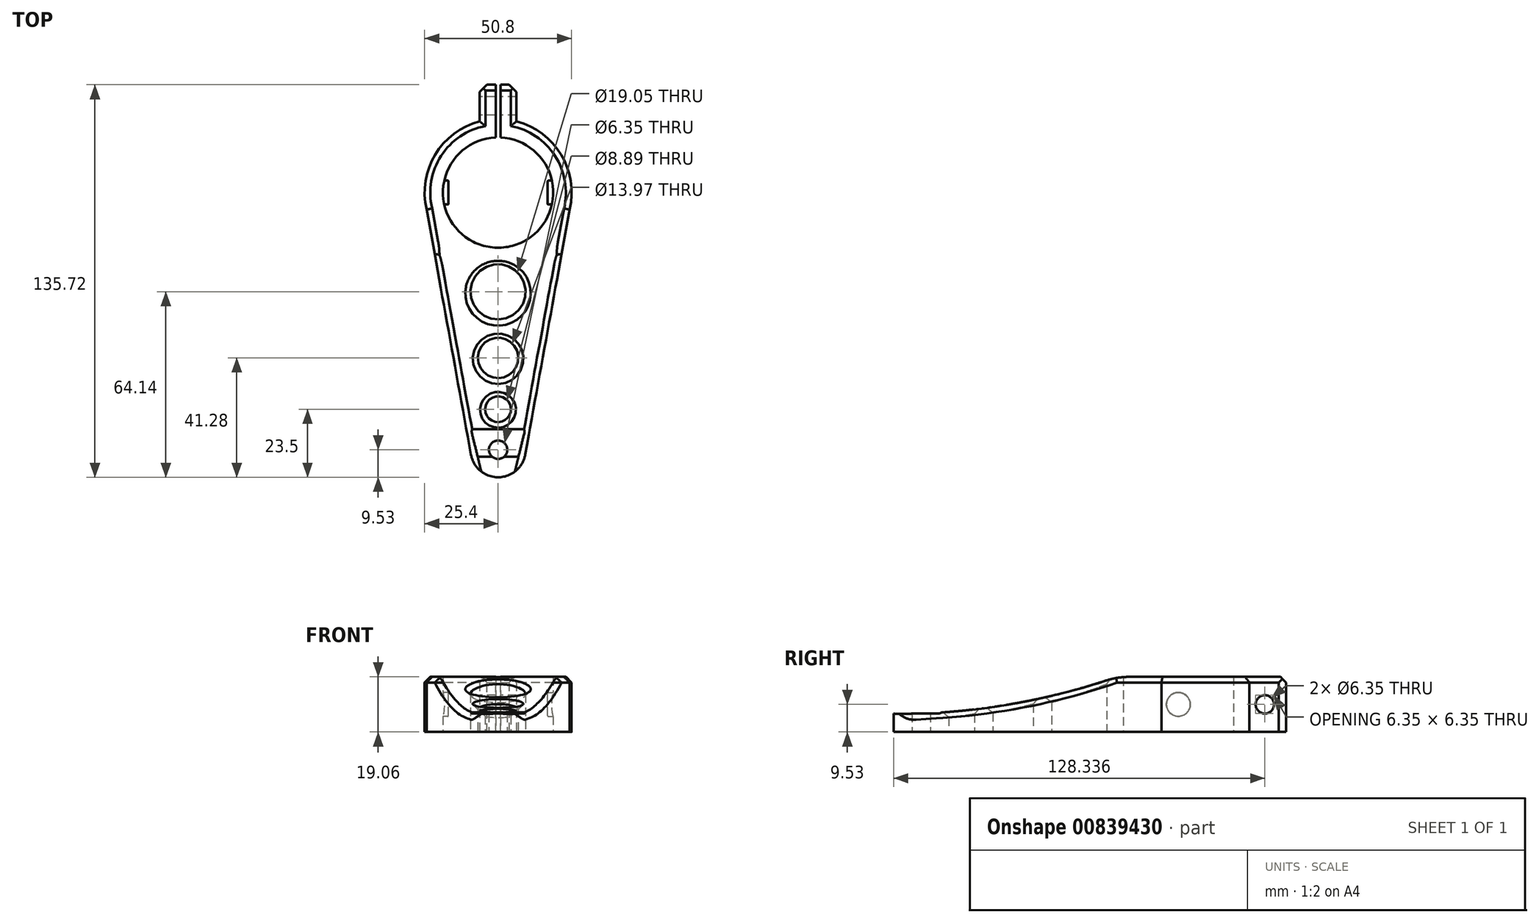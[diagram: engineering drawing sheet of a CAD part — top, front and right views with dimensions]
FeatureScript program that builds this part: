
annotation { "Feature Type Name" : "Feature", "Feature Type Description" : "" }
export const myFeature = defineFeature(function(context is Context, id is Id, definition is map)
    precondition{}
    {
        {
            var Q0;
            Q0=qCreatedBy(makeId("Top.planeOp"),FACE);
            var sketch = newSketch(context, id + "F0", { "sketchPlane" : qUnion([Q0])});
            skCircle(sketch, "E0", {"center": v(0, 0) * mm, "radius": 19.05 * mm});
            skCircle(sketch, "E1", {"center": v(0, 0) * mm, "radius": 25.4 * mm});
            skLineSegment(sketch, "E2", {"start": v(0, 0) * mm, "end": v(0, -88.9) * mm, "construction": true});
            skCircle(sketch, "E3", {"center": v(0, -88.9) * mm, "radius": 3.18 * mm});
            skCircle(sketch, "E4", {"center": v(0, -88.9) * mm, "radius": 9.53 * mm});
            skLineSegment(sketch, "E5", {"start": v(-24.71, -5.87) * mm, "end": v(-9.37, -90.6) * mm});
            skLineSegment(sketch, "E6.MirrorCS", {"start": v(24.71, -5.87) * mm, "end": v(9.37, -90.6) * mm});
            skCircle(sketch, "E7", {"center": v(0, -34.29) * mm, "radius": 9.53 * mm});
            skCircle(sketch, "E8", {"center": v(0, -57.15) * mm, "radius": 6.99 * mm});
            skCircle(sketch, "E9", {"center": v(0, -74.93) * mm, "radius": 4.45 * mm});
            skLineSegment(sketch, "E10", {"start": v(0, 0) * mm, "end": v(0, 30.94) * mm, "construction": true});
            skLineSegment(sketch, "E11.bottom", {"start": v(6.35, 24.6) * mm, "end": v(-6.35, 24.6) * mm});
            skLineSegment(sketch, "E11.top", {"start": v(6.35, 37.3) * mm, "end": v(-6.35, 37.3) * mm});
            skLineSegment(sketch, "E11.left", {"start": v(6.35, 24.6) * mm, "end": v(6.35, 37.3) * mm});
            skLineSegment(sketch, "E11.right", {"start": v(-6.35, 24.6) * mm, "end": v(-6.35, 37.3) * mm});
            skPoint(sketch, "E11.middle", {"position": v(0, 30.94) * mm});
            skSolve(sketch);
        }
        {
            var Q0;
            Q0 = qSketchRegion(id + "F0", true);
            extrude(context, id + "F1", {"entities" : qUnion([Q0]), "depth" : 19.05 * mm, "offsetDistance" : 25.4 * mm, "symmetric" : true});
        }
        {
            var Q0;
            Q0=qCreatedBy(makeId("Right.planeOp"),FACE);
            var sketch = newSketch(context, id + "F2", { "sketchPlane" : qUnion([Q0])});
            skLineSegment(sketch, "E12", {"start": v(0, 0) * mm, "end": v(-12.7, 0) * mm, "construction": true});
            skLineSegment(sketch, "E13", {"start": v(-12.7, 0) * mm, "end": v(-12.7, 12.7) * mm, "construction": true});
            skLineSegment(sketch, "E14", {"start": v(-12.7, 0) * mm, "end": v(-12.7, -12.7) * mm, "construction": true});
            skFitSpline(sketch, "E15", {"points": [v(-12.7, 12.7) * mm, v(-99.37, -3.18) * mm], "startDerivative": vector(-81.6, -32.58) * mm, "endDerivative": vector(-83.24, 1.78) * mm});
            skLineSegment(sketch, "E16", {"start": v(-99.37, -3.18) * mm, "end": v(-99.37, 12.7) * mm});
            skLineSegment(sketch, "E17", {"start": v(-99.37, 12.7) * mm, "end": v(-12.7, 12.7) * mm});
            skLineSegment(sketch, "E18.bottom", {"start": v(-81.84, 19.28) * mm, "end": v(-103.5, 19.28) * mm});
            skLineSegment(sketch, "E18.top", {"start": v(-81.84, -3.18) * mm, "end": v(-103.5, -3.18) * mm});
            skLineSegment(sketch, "E18.left", {"start": v(-81.84, 19.28) * mm, "end": v(-81.84, -3.17) * mm});
            skLineSegment(sketch, "E18.right", {"start": v(-103.5, 19.28) * mm, "end": v(-103.5, -3.18) * mm});
            skSolve(sketch);
        }
        {
            var Q0;
            Q0 = qSketchRegion(id + "F2", true);
            extrude(context, id + "F3", {"entities" : qUnion([Q0]), "operationType" : NewBodyOperationType.REMOVE, "endBound" : BoundingType.THROUGH_ALL, "oppositeDirection" : true, "depth" : 25.4 * mm, "offsetDistance" : 25.4 * mm, "hasSecondDirection" : true, "secondDirectionBound" : BoundingType.THROUGH_ALL, "secondDirectionOppositeDirection" : false, "secondDirectionDepth" : 25.4 * mm});
        }
        {
            var Q0;
            Q0=makeQuery(id+"F3.boolean.opBoolean","INTERSECT",EDGE,{"derivedFrom":[makeQuery(id+"F1.opExtrude","SWEPT_FACE",FACE,{"disambiguationData":[OSD([sQuery(id+"F0.wireOp",EDGE,"E5")])]}),makeQuery(id+"F3.opExtrude","SWEPT_FACE",FACE,{"disambiguationData":[OSD([sQuery(id+"F2.wireOp",EDGE,"E15")])]})]});
            var Q1;
            Q1=makeQuery(id+"F1.opExtrude","CAP_EDGE",EDGE,{"disambiguationData":[OSD([sQuery(id+"F0.wireOp",EDGE,"E5")])],"isStart":false});
            var Q2;
            {var subQ0=sQuery(id+"F0.wireOp",EDGE,"E1");Q2=makeQuery(id+"F1.opExtrude","CAP_EDGE",EDGE,{"disambiguationData":[OSD([subQ0]),TDD([makeQuery(id+"F0.imprint","IMPRINT",EDGE,{"disambiguationData":[TD([[makeQuery(id+"F0.imprint","INTERSECT",VERTEX,{"derivedFrom":[subQ0,sQuery(id+"F0.wireOp",EDGE,"E5")]}),1.0]])],"derivedFrom":subQ0})])],"isStart":false});}
            var Q3;
            Q3=makeQuery(id+"F1.opExtrude","CAP_EDGE",EDGE,{"disambiguationData":[OSD([sQuery(id+"F0.wireOp",EDGE,"E11.right")])],"isStart":false});
            var Q4;
            Q4=makeQuery(id+"F1.opExtrude","CAP_EDGE",EDGE,{"disambiguationData":[OSD([sQuery(id+"F0.wireOp",EDGE,"E11.top")])],"isStart":false});
            var Q5;
            Q5=makeQuery(id+"F1.opExtrude","CAP_EDGE",EDGE,{"disambiguationData":[OSD([sQuery(id+"F0.wireOp",EDGE,"E11.left")])],"isStart":false});
            var Q6;
            {var subQ0=sQuery(id+"F0.wireOp",EDGE,"E1");Q6=makeQuery(id+"F1.opExtrude","CAP_EDGE",EDGE,{"disambiguationData":[OSD([subQ0]),TDD([makeQuery(id+"F0.imprint","IMPRINT",EDGE,{"disambiguationData":[TD([[makeQuery(id+"F0.imprint","INTERSECT",VERTEX,{"derivedFrom":[subQ0,sQuery(id+"F0.wireOp",EDGE,"E6.MirrorCS")]}),-1.0]])],"derivedFrom":subQ0})])],"isStart":false});}
            var Q7;
            Q7=makeQuery(id+"F1.opExtrude","CAP_EDGE",EDGE,{"disambiguationData":[OSD([sQuery(id+"F0.wireOp",EDGE,"E6.MirrorCS")])],"isStart":false});
            var Q8;
            {var subQ0=sQuery(id+"F2.wireOp",EDGE,"E15");Q8=makeQuery(id+"F3.boolean.opBoolean","INTERSECT",EDGE,{"derivedFrom":[makeQuery(id+"F1.opExtrude","SWEPT_FACE",FACE,{"disambiguationData":[OSD([sQuery(id+"F0.wireOp",EDGE,"E6.MirrorCS")])]}),makeQuery(id+"F3.opExtrude","SWEPT_FACE",FACE,{"disambiguationData":[OSD([subQ0]),TDD([makeQuery(id+"F2.imprint","IMPRINT",EDGE,{"disambiguationData":[TD([[makeQuery(id+"F2.imprint","INTERSECT",VERTEX,{"derivedFrom":[subQ0,sQuery(id+"F2.wireOp",EDGE,"E17")]}),-1.0]])],"derivedFrom":subQ0})])]})]});}
            chamfer(context, id + "F4", {"entities" : qUnion([Q0, Q1, Q2, Q3, Q4, Q5, Q6, Q7, Q8]), "width" : 1.9 * mm, "tangentPropagation" : true});
        }
        {
            var Q0;
            Q0=makeQuery(id+"F1.opExtrude","SWEPT_EDGE",EDGE,{"disambiguationData":[OSD([sQuery(id+"F0.wireOp",EDGE,"E11.top"),sQuery(id+"F0.wireOp",EDGE,"E11.right")])]});
            var Q1;
            Q1=makeQuery(id+"F1.opExtrude","SWEPT_EDGE",EDGE,{"disambiguationData":[OSD([sQuery(id+"F0.wireOp",EDGE,"E11.top"),sQuery(id+"F0.wireOp",EDGE,"E11.left")])]});
            chamfer(context, id + "F5", {"entities" : qUnion([Q0, Q1]), "width" : 2.54 * mm, "tangentPropagation" : true});
        }
        {
            var Q0;
            Q0=qCreatedBy(makeId("Right.planeOp"),FACE);
            var sketch = newSketch(context, id + "F6", { "sketchPlane" : qUnion([Q0])});
            skLineSegment(sketch, "E19.bottom", {"start": v(48.1, -21.83) * mm, "end": v(8.61, -21.83) * mm});
            skLineSegment(sketch, "E19.top", {"start": v(48.1, 18.76) * mm, "end": v(8.61, 18.76) * mm});
            skLineSegment(sketch, "E19.left", {"start": v(48.1, -21.83) * mm, "end": v(48.1, 18.76) * mm});
            skLineSegment(sketch, "E19.right", {"start": v(8.61, -21.83) * mm, "end": v(8.61, 18.76) * mm});
            skSolve(sketch);
        }
        {
            var Q0;
            Q0 = qSketchRegion(id + "F6", true);
            extrude(context, id + "F7", {"entities" : qUnion([Q0]), "operationType" : NewBodyOperationType.REMOVE, "oppositeDirection" : true, "depth" : 1.65 * mm, "offsetDistance" : 25.4 * mm, "symmetric" : true});
        }
        {
            var Q0;
            Q0=makeQuery(id+"F3.boolean.opBoolean","INTERSECT",EDGE,{"derivedFrom":[makeQuery(id+"F1.opExtrude","SWEPT_FACE",FACE,{"disambiguationData":[OSD([sQuery(id+"F0.wireOp",EDGE,"E7")])]}),makeQuery(id+"F3.opExtrude","SWEPT_FACE",FACE,{"disambiguationData":[OSD([sQuery(id+"F2.wireOp",EDGE,"E15")])]})]});
            var Q1;
            Q1=makeQuery(id+"F3.boolean.opBoolean","INTERSECT",EDGE,{"derivedFrom":[makeQuery(id+"F1.opExtrude","SWEPT_FACE",FACE,{"disambiguationData":[OSD([sQuery(id+"F0.wireOp",EDGE,"E8")])]}),makeQuery(id+"F3.opExtrude","SWEPT_FACE",FACE,{"disambiguationData":[OSD([sQuery(id+"F2.wireOp",EDGE,"E15")])]})]});
            var Q2;
            Q2=makeQuery(id+"F3.boolean.opBoolean","INTERSECT",EDGE,{"derivedFrom":[makeQuery(id+"F1.opExtrude","SWEPT_FACE",FACE,{"disambiguationData":[OSD([sQuery(id+"F0.wireOp",EDGE,"E9")])]}),makeQuery(id+"F3.opExtrude","SWEPT_FACE",FACE,{"disambiguationData":[OSD([sQuery(id+"F2.wireOp",EDGE,"E15")])]})]});
            var Q3;
            Q3=makeQuery(id+"F3.boolean.opBoolean","INTERSECT",EDGE,{"derivedFrom":[makeQuery(id+"F1.opExtrude","SWEPT_FACE",FACE,{"disambiguationData":[OSD([sQuery(id+"F0.wireOp",EDGE,"E7")])]}),makeQuery(id+"F3.opExtrude","SWEPT_FACE",FACE,{"disambiguationData":[OSD([sQuery(id+"F2.wireOp",EDGE,"91bf1d3f-22a0-42a9-8744-9027ca880ea70.MirrorCS")])]})]});
            var Q4;
            Q4=makeQuery(id+"F3.boolean.opBoolean","INTERSECT",EDGE,{"derivedFrom":[makeQuery(id+"F1.opExtrude","SWEPT_FACE",FACE,{"disambiguationData":[OSD([sQuery(id+"F0.wireOp",EDGE,"E8")])]}),makeQuery(id+"F3.opExtrude","SWEPT_FACE",FACE,{"disambiguationData":[OSD([sQuery(id+"F2.wireOp",EDGE,"91bf1d3f-22a0-42a9-8744-9027ca880ea70.MirrorCS")])]})]});
            var Q5;
            Q5=makeQuery(id+"F3.boolean.opBoolean","INTERSECT",EDGE,{"derivedFrom":[makeQuery(id+"F1.opExtrude","SWEPT_FACE",FACE,{"disambiguationData":[OSD([sQuery(id+"F0.wireOp",EDGE,"E9")])]}),makeQuery(id+"F3.opExtrude","SWEPT_FACE",FACE,{"disambiguationData":[OSD([sQuery(id+"F2.wireOp",EDGE,"91bf1d3f-22a0-42a9-8744-9027ca880ea70.MirrorCS")])]})]});
            chamfer(context, id + "F8", {"entities" : qUnion([Q0, Q1, Q2, Q3, Q4, Q5]), "width" : 1.78 * mm, "tangentPropagation" : true});
        }
        {
            var Q0;
            Q0=makeQuery(id+"F1.opExtrude","SWEPT_FACE",FACE,{"disambiguationData":[OSD([sQuery(id+"F0.wireOp",EDGE,"E11.right")])]});
            var sketch = newSketch(context, id + "F9", { "sketchPlane" : qUnion([Q0])});
            skCircle(sketch, "E20", {"center": v(-29.9, 0) * mm, "radius": 3.18 * mm});
            skSolve(sketch);
        }
        {
            var Q0;
            Q0 = qSketchRegion(id + "F9", true);
            extrude(context, id + "F10", {"entities" : qUnion([Q0]), "operationType" : NewBodyOperationType.REMOVE, "oppositeDirection" : true, "depth" : 25.4 * mm, "offsetDistance" : 25.4 * mm, "hasSecondDirection" : true, "secondDirectionOppositeDirection" : false, "secondDirectionDepth" : 25.4 * mm});
        }
        {
            var Q0;
            Q0=makeQuery(id+"F3.boolean.opBoolean","INTERSECT",EDGE,{"derivedFrom":[makeQuery(id+"F1.opExtrude","CAP_FACE",FACE,{"disambiguationData":[OSD([sQuery(id+"F0.wireOp",EDGE,"E0"),sQuery(id+"F0.wireOp",EDGE,"E1"),sQuery(id+"F0.wireOp",EDGE,"E3"),sQuery(id+"F0.wireOp",EDGE,"E4"),sQuery(id+"F0.wireOp",EDGE,"E5"),sQuery(id+"F0.wireOp",EDGE,"E6.MirrorCS"),sQuery(id+"F0.wireOp",EDGE,"E7"),sQuery(id+"F0.wireOp",EDGE,"E8"),sQuery(id+"F0.wireOp",EDGE,"E9"),sQuery(id+"F0.wireOp",EDGE,"E11.top"),sQuery(id+"F0.wireOp",EDGE,"E11.left"),sQuery(id+"F0.wireOp",EDGE,"E11.right")])],"isStart":true}),makeQuery(id+"F3.opExtrude","SWEPT_FACE",FACE,{"disambiguationData":[OSD([sQuery(id+"F2.wireOp",EDGE,"91bf1d3f-22a0-42a9-8744-9027ca880ea70.MirrorCS")])]})]});
            var Q1;
            Q1=makeQuery(id+"F3.boolean.opBoolean","INTERSECT",EDGE,{"derivedFrom":[makeQuery(id+"F1.opExtrude","CAP_FACE",FACE,{"disambiguationData":[OSD([sQuery(id+"F0.wireOp",EDGE,"E0"),sQuery(id+"F0.wireOp",EDGE,"E1"),sQuery(id+"F0.wireOp",EDGE,"E3"),sQuery(id+"F0.wireOp",EDGE,"E4"),sQuery(id+"F0.wireOp",EDGE,"E5"),sQuery(id+"F0.wireOp",EDGE,"E6.MirrorCS"),sQuery(id+"F0.wireOp",EDGE,"E7"),sQuery(id+"F0.wireOp",EDGE,"E8"),sQuery(id+"F0.wireOp",EDGE,"E9"),sQuery(id+"F0.wireOp",EDGE,"E11.top"),sQuery(id+"F0.wireOp",EDGE,"E11.left"),sQuery(id+"F0.wireOp",EDGE,"E11.right")])],"isStart":false}),makeQuery(id+"F3.opExtrude","SWEPT_FACE",FACE,{"disambiguationData":[OSD([sQuery(id+"F2.wireOp",EDGE,"E15")])]})]});
            fillet(context, id + "F11", {"entities" : qUnion([Q0, Q1]), "tangentPropagation" : true, "radius" : 25.4 * mm, "defaultsChanged" : false, "vertexSettings" : [], "allowEdgeOverflow" : false});
        }
        {
            var Q0;
            Q0=qCreatedBy(makeId("Right.planeOp"),FACE);
            cPlane(context, id + "F12", {"entities" : qUnion([Q0]), "cplaneType" : CPlaneType.OFFSET, "offset" : 20.32 * mm, "width" : 152.4 * mm, "height" : 152.4 * mm});
        }
        {
            var Q0;
            Q0=qCreatedBy(makeId("Right.planeOp"),FACE);
            cPlane(context, id + "F13", {"entities" : qUnion([Q0]), "cplaneType" : CPlaneType.OFFSET, "offset" : 20.32 * mm, "oppositeDirection" : true, "width" : 152.4 * mm, "height" : 152.4 * mm});
        }
        {
            var Q0;
            Q0=qCreatedBy(id+"F12.planeOp",FACE);
            var sketch = newSketch(context, id + "F14", { "sketchPlane" : qUnion([Q0])});
            skCircle(sketch, "E21", {"center": v(0, 0) * mm, "radius": 4.13 * mm});
            skSolve(sketch);
        }
        {
            var Q0;
            Q0 = qSketchRegion(id + "F14", true);
            extrude(context, id + "F15", {"entities" : qUnion([Q0]), "operationType" : NewBodyOperationType.ADD, "oppositeDirection" : true, "depth" : 3.17 * mm, "offsetDistance" : 25.4 * mm});
        }
        {
            var Q0;
            Q0=qCreatedBy(id+"F13.planeOp",FACE);
            var sketch = newSketch(context, id + "F16", { "sketchPlane" : qUnion([Q0])});
            skCircle(sketch, "E22", {"center": v(0, 0) * mm, "radius": 4.13 * mm});
            skSolve(sketch);
        }
        {
            var Q0;
            Q0 = qSketchRegion(id + "F16", true);
            extrude(context, id + "F17", {"entities" : qUnion([Q0]), "operationType" : NewBodyOperationType.ADD, "depth" : 3.17 * mm, "offsetDistance" : 25.4 * mm});
        }
        {
            var Q0;
            Q0=makeQuery(id+"F15.opExtrude","CAP_EDGE",EDGE,{"disambiguationData":[OSD([sQuery(id+"F14.wireOp",EDGE,"E21")])],"isStart":false});
            var Q1;
            Q1=makeQuery(id+"F17.opExtrude","CAP_EDGE",EDGE,{"disambiguationData":[OSD([sQuery(id+"F16.wireOp",EDGE,"E22")])],"isStart":false});
            fillet(context, id + "F18", {"entities" : qUnion([Q0, Q1]), "tangentPropagation" : true, "radius" : 0.25 * mm, "defaultsChanged" : false, "vertexSettings" : [], "allowEdgeOverflow" : false});
        }
        {
            var Q0;
            Q0=makeQuery(id+"F3.boolean.opBoolean","COPY",EDGE,{"derivedFrom":makeQuery(id+"F3.opExtrude","SWEPT_EDGE",EDGE,{"disambiguationData":[OSD([sQuery(id+"F2.wireOp",EDGE,"E18.top"),sQuery(id+"F2.wireOp",EDGE,"E18.left")])]})});
            fillet(context, id + "F19", {"entities" : qUnion([Q0]), "tangentPropagation" : true, "radius" : 2.54 * mm, "defaultsChanged" : true, "vertexSettings" : [], "allowEdgeOverflow" : false});
        }
    });
